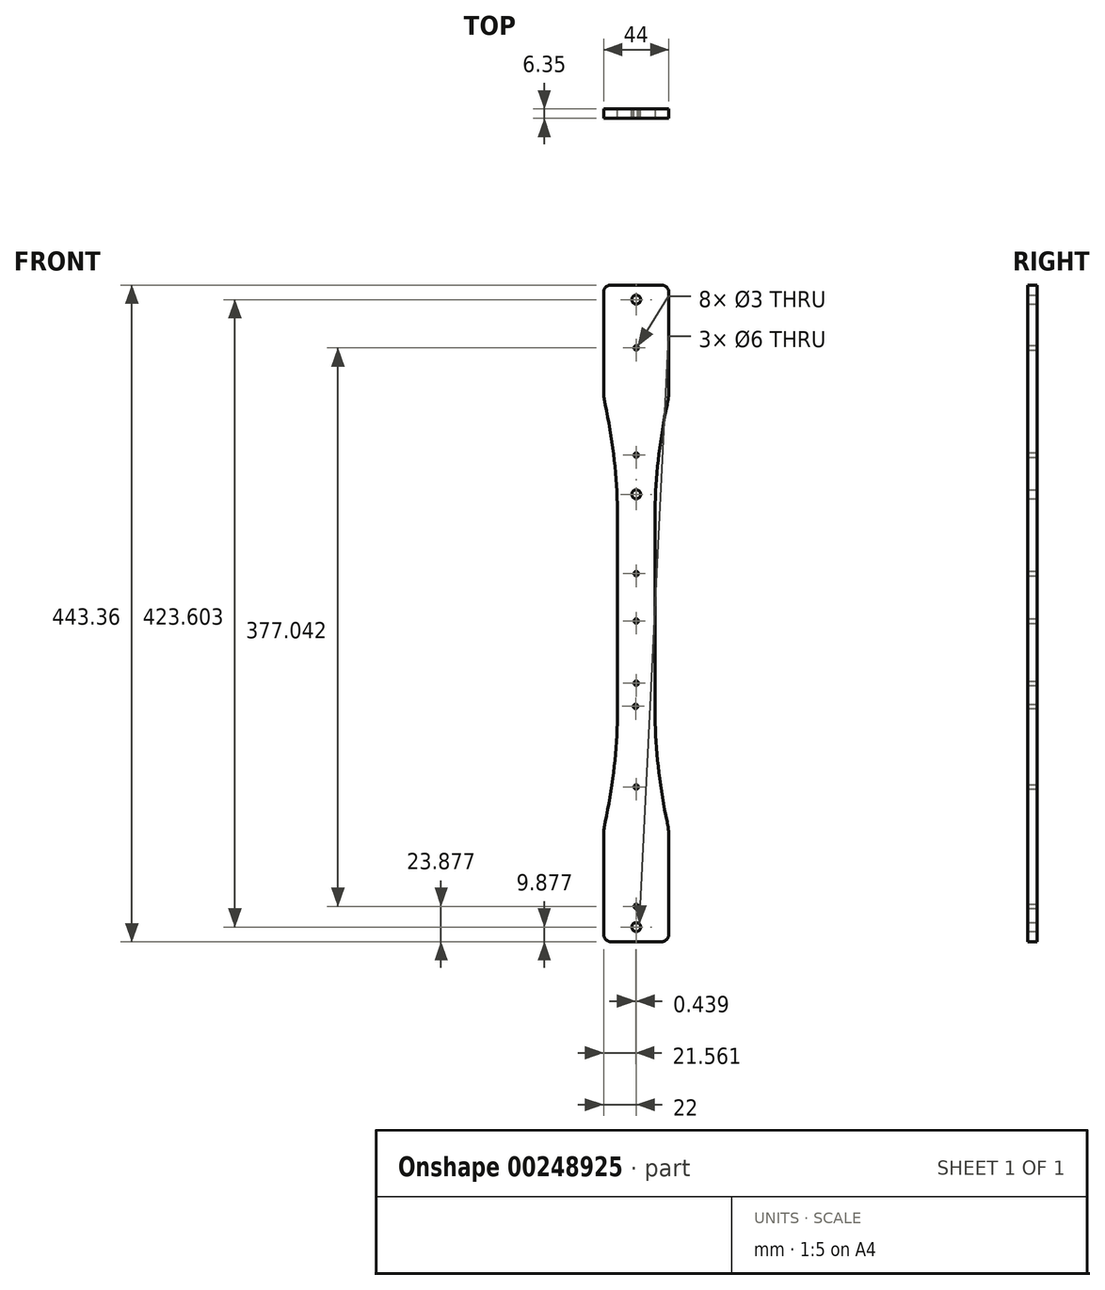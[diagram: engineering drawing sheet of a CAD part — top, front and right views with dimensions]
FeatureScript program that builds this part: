
annotation { "Feature Type Name" : "Feature", "Feature Type Description" : "" }
export const myFeature = defineFeature(function(context is Context, id is Id, definition is map)
    precondition{}
    {
        {
            var Q0;
            Q0=qCreatedBy(makeId("Front.planeOp"),FACE);
            var sketch = newSketch(context, id + "F0", { "sketchPlane" : qUnion([Q0])});
            skCircle(sketch, "E0", {"center": v(0, -85.45) * mm, "radius": 1.5 * mm});
            skCircle(sketch, "E1", {"center": v(-0.44, -31.05) * mm, "radius": 1.5 * mm});
            skCircle(sketch, "E2", {"center": v(0, 26.55) * mm, "radius": 1.5 * mm});
            skLineSegment(sketch, "E3.top", {"start": v(-4.69, -189.96) * mm, "end": v(4.69, -189.96) * mm});
            skPoint(sketch, "E4.visualSharp", {"position": v(12.7, -189.96) * mm});
            skPoint(sketch, "E5.visualSharp", {"position": v(-12.7, -189.96) * mm});
            skCircle(sketch, "E6", {"center": v(0, 58.56) * mm, "radius": 1.5 * mm});
            skLineSegment(sketch, "E7", {"start": v(0, 26.55) * mm, "end": v(0, 99.81) * mm, "construction": true});
            skLineSegment(sketch, "E8", {"start": v(0, 99.81) * mm, "end": v(0, -85.45) * mm, "construction": true});
            skLineSegment(sketch, "E9", {"start": v(0, -85.45) * mm, "end": v(0, -201.73) * mm, "construction": true});
            skCircle(sketch, "E10", {"center": v(0, 243.52) * mm, "radius": 3 * mm});
            skCircle(sketch, "E11", {"center": v(0, -15.45) * mm, "radius": 1.5 * mm});
            skLineSegment(sketch, "E12", {"start": v(0, 58.56) * mm, "end": v(0, 424.12) * mm});
            skCircle(sketch, "E13", {"center": v(0, 210.96) * mm, "radius": 1.5 * mm});
            skCircle(sketch, "E14", {"center": v(0, 138.56) * mm, "radius": 1.5 * mm});
            skLineSegment(sketch, "E15", {"start": v(12.7, 31.72) * mm, "end": v(-12.7, 31.72) * mm, "construction": true});
            skLineSegment(sketch, "E16.MirrorCS", {"start": v(-4.69, 253.4) * mm, "end": v(4.69, 253.4) * mm});
            skPoint(sketch, "E17.orphan", {"position": v(-7.5, 253.51) * mm});
            skPoint(sketch, "E18.start.orphan", {"position": v(7.5, 253.51) * mm});
            skCircle(sketch, "E19", {"center": v(0, -180.08) * mm, "radius": 3 * mm});
            skCircle(sketch, "E20", {"center": v(0, 112.09) * mm, "radius": 3 * mm});
            skLineSegment(sketch, "E21.trimOffspring", {"start": v(-12.7, 104.8) * mm, "end": v(-12.7, -41.36) * mm});
            skLineSegment(sketch, "E22.trimOffspring", {"start": v(12.7, 104.8) * mm, "end": v(12.7, -41.36) * mm});
            skLineSegment(sketch, "E23", {"start": v(-22, 177.54) * mm, "end": v(-22, 236.3) * mm});
            skLineSegment(sketch, "E24.MirrorCS", {"start": v(22, 177.54) * mm, "end": v(22, 236.3) * mm});
            skArc(sketch, "E25", {"start": v(-12.7, 104.8) * mm, "mid": v(-15.58, 141.4) * mm, "end": v(-22, 177.54) * mm});
            skArc(sketch, "E26.MirrorCS", {"start": v(12.7, 104.8) * mm, "mid": v(15.58, 141.4) * mm, "end": v(22, 177.54) * mm});
            skPoint(sketch, "E27.orphan", {"position": v(-4.69, 253.4) * mm});
            skPoint(sketch, "E28.orphan", {"position": v(-22, 240.87) * mm});
            skPoint(sketch, "E29.orphan", {"position": v(4.69, 253.4) * mm});
            skPoint(sketch, "E30.orphan", {"position": v(22, 240.87) * mm});
            skLineSegment(sketch, "E31", {"start": v(0, 253.4) * mm, "end": v(-22, 253.4) * mm});
            skLineSegment(sketch, "E32", {"start": v(-22, 225.43) * mm, "end": v(-22, 253.4) * mm});
            skLineSegment(sketch, "E33.MirrorCS", {"start": v(22, 225.43) * mm, "end": v(22, 253.4) * mm});
            skLineSegment(sketch, "E34.MirrorCS", {"start": v(0, 253.4) * mm, "end": v(22, 253.4) * mm});
            skArc(sketch, "E35.MirrorCS", {"start": v(12.7, -41.36) * mm, "mid": v(15.58, -77.96) * mm, "end": v(22, -114.1) * mm});
            skLineSegment(sketch, "E36.MirrorCS", {"start": v(22, -114.1) * mm, "end": v(22, -172.87) * mm});
            skArc(sketch, "E37.MirrorCS", {"start": v(-12.7, -41.36) * mm, "mid": v(-15.58, -77.96) * mm, "end": v(-22, -114.1) * mm});
            skLineSegment(sketch, "E38.MirrorCS", {"start": v(-22, -114.1) * mm, "end": v(-22, -172.87) * mm});
            skLineSegment(sketch, "E39.MirrorCS", {"start": v(0, -189.96) * mm, "end": v(-22, -189.96) * mm});
            skLineSegment(sketch, "E40.MirrorCS", {"start": v(0, -189.96) * mm, "end": v(22, -189.96) * mm});
            skLineSegment(sketch, "E41.MirrorCS", {"start": v(22, -162) * mm, "end": v(22, -189.96) * mm});
            skLineSegment(sketch, "E42.MirrorCS", {"start": v(-22, -162) * mm, "end": v(-22, -189.96) * mm});
            skCircle(sketch, "E43", {"center": v(0, -166.08) * mm, "radius": 1.5 * mm});
            skSolve(sketch);
        }
        {
            var Q0;
            Q0=makeQuery(id+"F0.imprint","IMPRINT",FACE,{"disambiguationData":[TD([[makeQuery(id+"F0.imprint","IMPRINT",EDGE,{"derivedFrom":sQuery(id+"F0.wireOp",EDGE,"E0")}),-1.0]])]});
            var Q1;
            {var subQ8=sQuery(id+"F0.wireOp",EDGE,"E3.left");Q1=makeQuery(id+"F0.imprint","IMPRINT",FACE,{"disambiguationData":[TD([[makeQuery(id+"F0.imprint","IMPRINT",EDGE,{"derivedFrom":subQ8}),-1.0]])]});}
            var Q2;
            {var subQ10=sQuery(id+"F0.wireOp",EDGE,"E3.right");Q2=makeQuery(id+"F0.imprint","IMPRINT",FACE,{"disambiguationData":[TD([[makeQuery(id+"F0.imprint","IMPRINT",EDGE,{"derivedFrom":subQ10}),1.0]])]});}
            var Q3;
            {var subQ8=sQuery(id+"F0.wireOp",EDGE,"E3.right");Q3=makeQuery(id+"F0.imprint","IMPRINT",FACE,{"disambiguationData":[TD([[makeQuery(id+"F0.imprint","IMPRINT",EDGE,{"derivedFrom":subQ8}),-1.0]])]});}
            var Q4;
            {var subQ8=sQuery(id+"F0.wireOp",EDGE,"E3.left");Q4=makeQuery(id+"F0.imprint","IMPRINT",FACE,{"disambiguationData":[TD([[makeQuery(id+"F0.imprint","IMPRINT",EDGE,{"derivedFrom":subQ8}),1.0]])]});}
            var Q5;
            {var subQ0=sQuery(id+"F0.wireOp",EDGE,"ywFLEBLb-G5Qe-hJVo-9jNG-EmXgII5EXrAz");Q5=makeQuery(id+"F0.imprint","IMPRINT",FACE,{"disambiguationData":[TD([[makeQuery(id+"F0.imprint","IMPRINT",EDGE,{"derivedFrom":subQ0}),-1.0]])]});}
            var Q6;
            {var subQ17=sQuery(id+"F0.wireOp",EDGE,"E23");Q6=makeQuery(id+"F0.imprint","IMPRINT",FACE,{"disambiguationData":[TD([[makeQuery(id+"F0.imprint","IMPRINT",EDGE,{"derivedFrom":subQ17}),-1.0]])]});}
            var Q7;
            {var subQ4=sQuery(id+"F0.wireOp",EDGE,"E24.MirrorCS");Q7=makeQuery(id+"F0.imprint","IMPRINT",FACE,{"disambiguationData":[TD([[makeQuery(id+"F0.imprint","IMPRINT",EDGE,{"derivedFrom":subQ4}),1.0]])]});}
            var Q8;
            {var subQ2=sQuery(id+"F0.wireOp",EDGE,"E4.filletArc");Q8=makeQuery(id+"F0.imprint","IMPRINT",FACE,{"disambiguationData":[TD([[makeQuery(id+"F0.imprint","IMPRINT",EDGE,{"derivedFrom":subQ2}),-1.0]])]});}
            var Q9;
            {var subQ1=sQuery(id+"F0.wireOp",EDGE,"E4.filletArc");Q9=makeQuery(id+"F0.imprint","IMPRINT",FACE,{"disambiguationData":[TD([[makeQuery(id+"F0.imprint","IMPRINT",EDGE,{"derivedFrom":subQ1}),1.0]])]});}
            extrude(context, id + "F1", {"entities" : qUnion([Q0, Q1, Q2, Q3, Q4, Q5, Q6, Q7, Q8, Q9]), "depth" : 6.35 * mm});
        }
        {
            var Q0;
            Q0=makeQuery(id+"F1.opExtrude","SWEPT_EDGE",EDGE,{"disambiguationData":[OSD([sQuery(id+"F0.wireOp",EDGE,"E31"),sQuery(id+"F0.wireOp",EDGE,"E32")])]});
            var Q1;
            Q1=makeQuery(id+"F1.opExtrude","SWEPT_EDGE",EDGE,{"disambiguationData":[OSD([sQuery(id+"F0.wireOp",EDGE,"E33.MirrorCS"),sQuery(id+"F0.wireOp",EDGE,"E34.MirrorCS")])]});
            var Q2;
            Q2=makeQuery(id+"F1.opExtrude","SWEPT_EDGE",EDGE,{"disambiguationData":[OSD([sQuery(id+"F0.wireOp",EDGE,"E40.MirrorCS"),sQuery(id+"F0.wireOp",EDGE,"E41.MirrorCS")])]});
            var Q3;
            Q3=makeQuery(id+"F1.opExtrude","SWEPT_EDGE",EDGE,{"disambiguationData":[OSD([sQuery(id+"F0.wireOp",EDGE,"E39.MirrorCS"),sQuery(id+"F0.wireOp",EDGE,"E42.MirrorCS")])]});
            fillet(context, id + "F2", {"entities" : qUnion([Q0, Q1, Q2, Q3]), "radius" : 5.08 * mm, "tangentPropagation" : true, "allowEdgeOverflow" : false});
        }
        {
            var Q0;
            Q0=makeQuery(id+"F1.opExtrude","SWEPT_EDGE",EDGE,{"disambiguationData":[OSD([sQuery(id+"F0.wireOp",EDGE,"E37.MirrorCS"),sQuery(id+"F0.wireOp",EDGE,"E38.MirrorCS")])]});
            var Q1;
            Q1=makeQuery(id+"F1.opExtrude","SWEPT_EDGE",EDGE,{"disambiguationData":[OSD([sQuery(id+"F0.wireOp",EDGE,"E35.MirrorCS"),sQuery(id+"F0.wireOp",EDGE,"E36.MirrorCS")])]});
            var Q2;
            Q2=makeQuery(id+"F1.opExtrude","SWEPT_EDGE",EDGE,{"disambiguationData":[OSD([sQuery(id+"F0.wireOp",EDGE,"E24.MirrorCS"),sQuery(id+"F0.wireOp",EDGE,"E26.MirrorCS")])]});
            var Q3;
            Q3=makeQuery(id+"F1.opExtrude","SWEPT_EDGE",EDGE,{"disambiguationData":[OSD([sQuery(id+"F0.wireOp",EDGE,"E23"),sQuery(id+"F0.wireOp",EDGE,"E25")])]});
            var Q4;
            Q4=makeQuery(id+"F1.opExtrude","SWEPT_EDGE",EDGE,{"disambiguationData":[OSD([sQuery(id+"F0.wireOp",EDGE,"E21.trimOffspring"),sQuery(id+"F0.wireOp",EDGE,"E25")])]});
            var Q5;
            Q5=makeQuery(id+"F1.opExtrude","SWEPT_EDGE",EDGE,{"disambiguationData":[OSD([sQuery(id+"F0.wireOp",EDGE,"E22.trimOffspring"),sQuery(id+"F0.wireOp",EDGE,"E26.MirrorCS")])]});
            var Q6;
            Q6=makeQuery(id+"F1.opExtrude","SWEPT_EDGE",EDGE,{"disambiguationData":[OSD([sQuery(id+"F0.wireOp",EDGE,"E22.trimOffspring"),sQuery(id+"F0.wireOp",EDGE,"E35.MirrorCS")])]});
            var Q7;
            Q7=makeQuery(id+"F1.opExtrude","SWEPT_EDGE",EDGE,{"disambiguationData":[OSD([sQuery(id+"F0.wireOp",EDGE,"E21.trimOffspring"),sQuery(id+"F0.wireOp",EDGE,"E37.MirrorCS")])]});
            fillet(context, id + "F3", {"entities" : qUnion([Q0, Q1, Q2, Q3, Q4, Q5, Q6, Q7]), "radius" : 50.8 * mm, "tangentPropagation" : true, "allowEdgeOverflow" : false});
        }
    });
